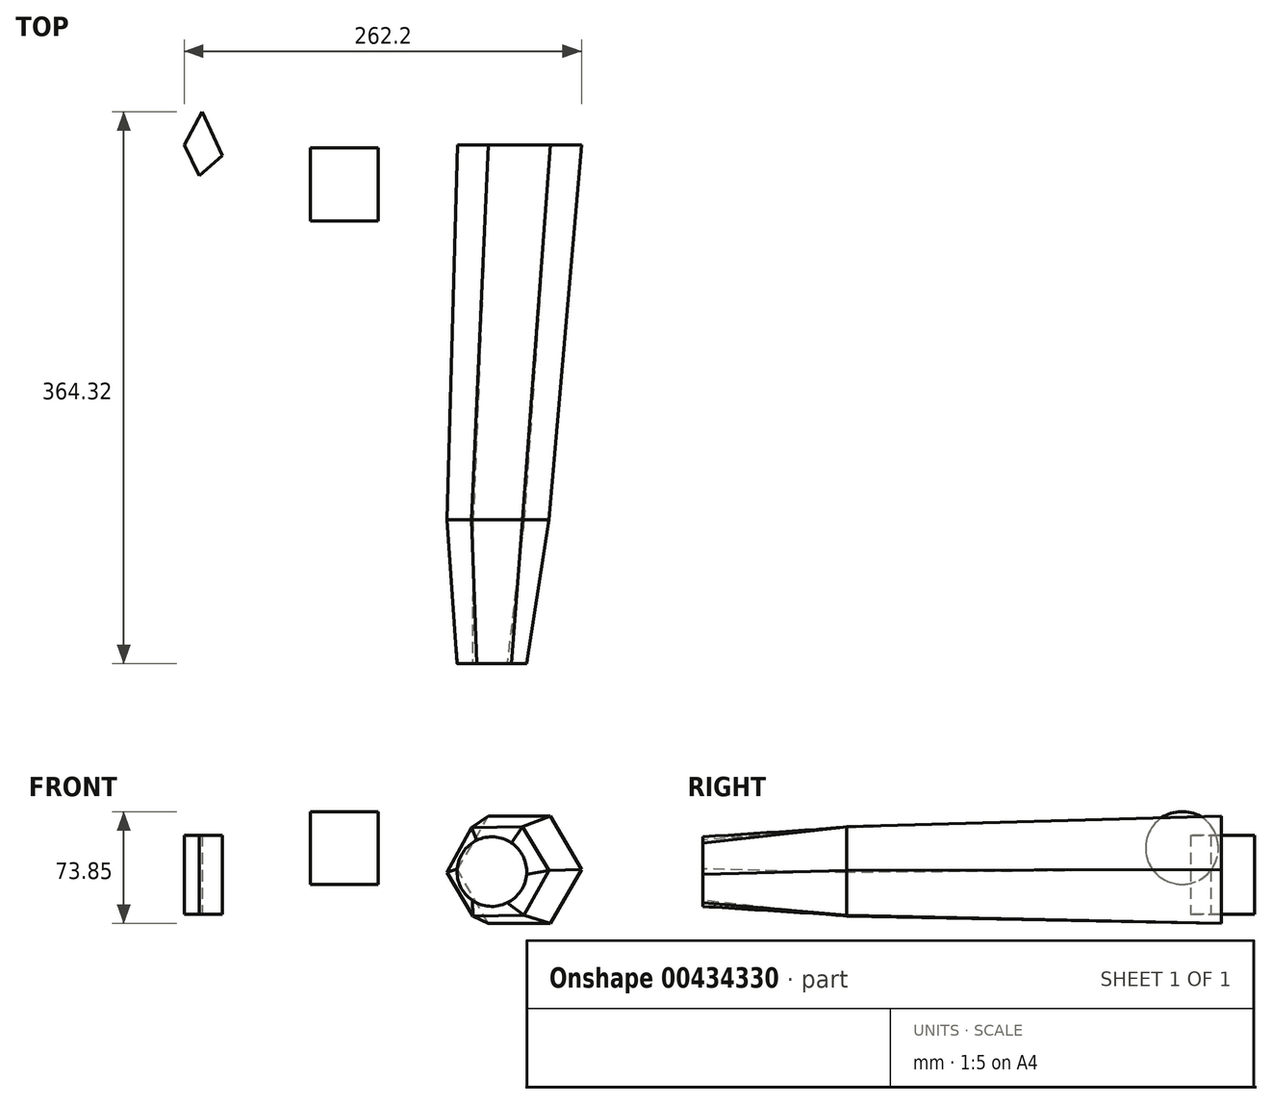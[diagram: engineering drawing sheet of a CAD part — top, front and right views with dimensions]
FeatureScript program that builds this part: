
annotation { "Feature Type Name" : "Feature", "Feature Type Description" : "" }
export const myFeature = defineFeature(function(context is Context, id is Id, definition is map)
    precondition{}
    {
        {
            var Q0;
            Q0=qCreatedBy(makeId("Top.planeOp"),FACE);
            var sketch = newSketch(context, id + "F0", { "sketchPlane" : qUnion([Q0])});
            skLineSegment(sketch, "E0", {"start": v(-118.12, -20.16) * mm, "end": v(-102.88, -6.98) * mm});
            skLineSegment(sketch, "E1", {"start": v(-102.88, -6.98) * mm, "end": v(-116.22, 21.93) * mm});
            skLineSegment(sketch, "E2", {"start": v(-116.22, 21.93) * mm, "end": v(-128.13, 0) * mm});
            skLineSegment(sketch, "E3", {"start": v(-128.13, 0) * mm, "end": v(-118.12, -20.16) * mm});
            skSolve(sketch);
        }
        {
            var Q0;
            Q0=makeQuery(id+"F0.imprint","IMPRINT",FACE,{"disambiguationData":[TD([[makeQuery(id+"F0.imprint","IMPRINT",EDGE,{"derivedFrom":sQuery(id+"F0.wireOp",EDGE,"E0")}),1.0]])]});
            extrude(context, id + "F1", {"entities" : qUnion([Q0]), "depth" : 52.07 * mm});
        }
        {
            var Q0;
            Q0=qCreatedBy(makeId("Right.planeOp"),FACE);
            var sketch = newSketch(context, id + "F2", { "sketchPlane" : qUnion([Q0])});
            skCircle(sketch, "E4", {"center": v(-25.98, 43.7) * mm, "radius": 24.03 * mm});
            skSolve(sketch);
        }
        {
            var Q0;
            Q0=makeQuery(id+"F2.imprint","IMPRINT",FACE,{"disambiguationData":[TD([[makeQuery(id+"F2.imprint","IMPRINT",EDGE,{"derivedFrom":sQuery(id+"F2.wireOp",EDGE,"E4")}),1.0]])]});
            extrude(context, id + "F3", {"entities" : qUnion([Q0]), "oppositeDirection" : true, "depth" : 44.96 * mm});
        }
        {
            var Q0;
            Q0=qCreatedBy(makeId("Front.planeOp"),FACE);
            var sketch = newSketch(context, id + "F4", { "sketchPlane" : qUnion([Q0])});
            skCircle(sketch, "E5.cCircle", {"center": v(93.1, 29.36) * mm, "radius": 35.47 * mm, "construction": true});
            skLineSegment(sketch, "E5.0", {"start": v(72.63, 64.83) * mm, "end": v(113.59, 64.83) * mm});
            skLineSegment(sketch, "E5.1", {"start": v(113.59, 64.83) * mm, "end": v(134.07, 29.36) * mm});
            skLineSegment(sketch, "E5.2", {"start": v(134.07, 29.36) * mm, "end": v(113.59, -6.1) * mm});
            skLineSegment(sketch, "E5.3", {"start": v(113.59, -6.1) * mm, "end": v(72.63, -6.1) * mm});
            skLineSegment(sketch, "E5.4", {"start": v(72.63, -6.1) * mm, "end": v(52.15, 29.36) * mm});
            skLineSegment(sketch, "E5.5", {"start": v(52.15, 29.36) * mm, "end": v(72.63, 64.83) * mm});
            skPoint(sketch, "E5.0.midPoint", {"position": v(93.1, 64.83) * mm});
            skSolve(sketch);
        }
        {
            var Q0;
            Q0=makeQuery(id+"F4.imprint","IMPRINT",FACE,{"disambiguationData":[TD([[makeQuery(id+"F4.imprint","IMPRINT",EDGE,{"derivedFrom":sQuery(id+"F4.wireOp",EDGE,"E5.0")}),-1.0]])]});
            cPlane(context, id + "F5", {"entities" : qUnion([Q0]), "cplaneType" : CPlaneType.OFFSET, "offset" : 247.4 * mm, "width" : 152.4 * mm, "height" : 152.4 * mm});
        }
        {
            var Q0;
            Q0=qCreatedBy(id+"F5.planeOp",FACE);
            var sketch = newSketch(context, id + "F6", { "sketchPlane" : qUnion([Q0])});
            skCircle(sketch, "E6.cCircle", {"center": v(78.82, 28.2) * mm, "radius": 29.15 * mm, "construction": true});
            skLineSegment(sketch, "E6.0", {"start": v(95.08, 57.66) * mm, "end": v(112.47, 28.84) * mm});
            skLineSegment(sketch, "E6.1", {"start": v(112.47, 28.84) * mm, "end": v(96.21, -0.62) * mm});
            skLineSegment(sketch, "E6.2", {"start": v(96.21, -0.62) * mm, "end": v(62.56, -1.27) * mm});
            skLineSegment(sketch, "E6.3", {"start": v(62.56, -1.27) * mm, "end": v(45.17, 27.54) * mm});
            skLineSegment(sketch, "E6.4", {"start": v(45.17, 27.54) * mm, "end": v(61.43, 57) * mm});
            skLineSegment(sketch, "E6.5", {"start": v(61.43, 57) * mm, "end": v(95.08, 57.66) * mm});
            skPoint(sketch, "E6.0.midPoint", {"position": v(103.78, 43.25) * mm});
            skSolve(sketch);
        }
        {
            var Q0;
            Q0=makeQuery(id+"F4.imprint","IMPRINT",FACE,{"disambiguationData":[TD([[makeQuery(id+"F4.imprint","IMPRINT",EDGE,{"derivedFrom":sQuery(id+"F4.wireOp",EDGE,"E5.0")}),-1.0]])]});
            var Q1;
            Q1=makeQuery(id+"F6.imprint","IMPRINT",FACE,{"disambiguationData":[TD([[makeQuery(id+"F6.imprint","IMPRINT",EDGE,{"derivedFrom":sQuery(id+"F6.wireOp",EDGE,"E6.0")}),-1.0]])]});
            loft(context, id + "F7", {"sheetProfilesArray" : [{ "sheetProfileEntities" : qUnion([Q0]) }, { "sheetProfileEntities" : qUnion([Q1]) }]});
        }
        {
            var Q0;
            Q0=qCreatedBy(id+"F5.planeOp",FACE);
            cPlane(context, id + "F8", {"entities" : qUnion([Q0]), "cplaneType" : CPlaneType.OFFSET, "offset" : 95 * mm, "width" : 152.4 * mm, "height" : 152.4 * mm});
        }
        {
            var Q0;
            Q0=qCreatedBy(id+"F8.planeOp",FACE);
            var sketch = newSketch(context, id + "F9", { "sketchPlane" : qUnion([Q0])});
            skCircle(sketch, "E7", {"center": v(74.93, 28.1) * mm, "radius": 22.96 * mm});
            skSolve(sketch);
        }
        {
            var Q1;
            Q1=makeQuery(id+"F7.opLoft","CAP_FACE",FACE,{"disambiguationData":[OSD([makeQuery(id+"F6.imprint","IMPRINT",FACE,{"disambiguationData":[TD([[makeQuery(id+"F6.imprint","IMPRINT",EDGE,{"derivedFrom":sQuery(id+"F6.wireOp",EDGE,"E6.0")}),-1.0]])]})])],"isStart":true});
            var Q2;
            Q2=makeQuery(id+"F9.imprint","IMPRINT",FACE,{"disambiguationData":[TD([[makeQuery(id+"F9.imprint","IMPRINT",EDGE,{"derivedFrom":sQuery(id+"F9.wireOp",EDGE,"E7")}),1.0]])]});
            loft(context, id + "F10", {"operationType" : NewBodyOperationType.ADD, "sheetProfilesArray" : [{ "sheetProfileEntities" : qUnion([Q1]) }, { "sheetProfileEntities" : qUnion([Q2]) }]});
        }
    });
